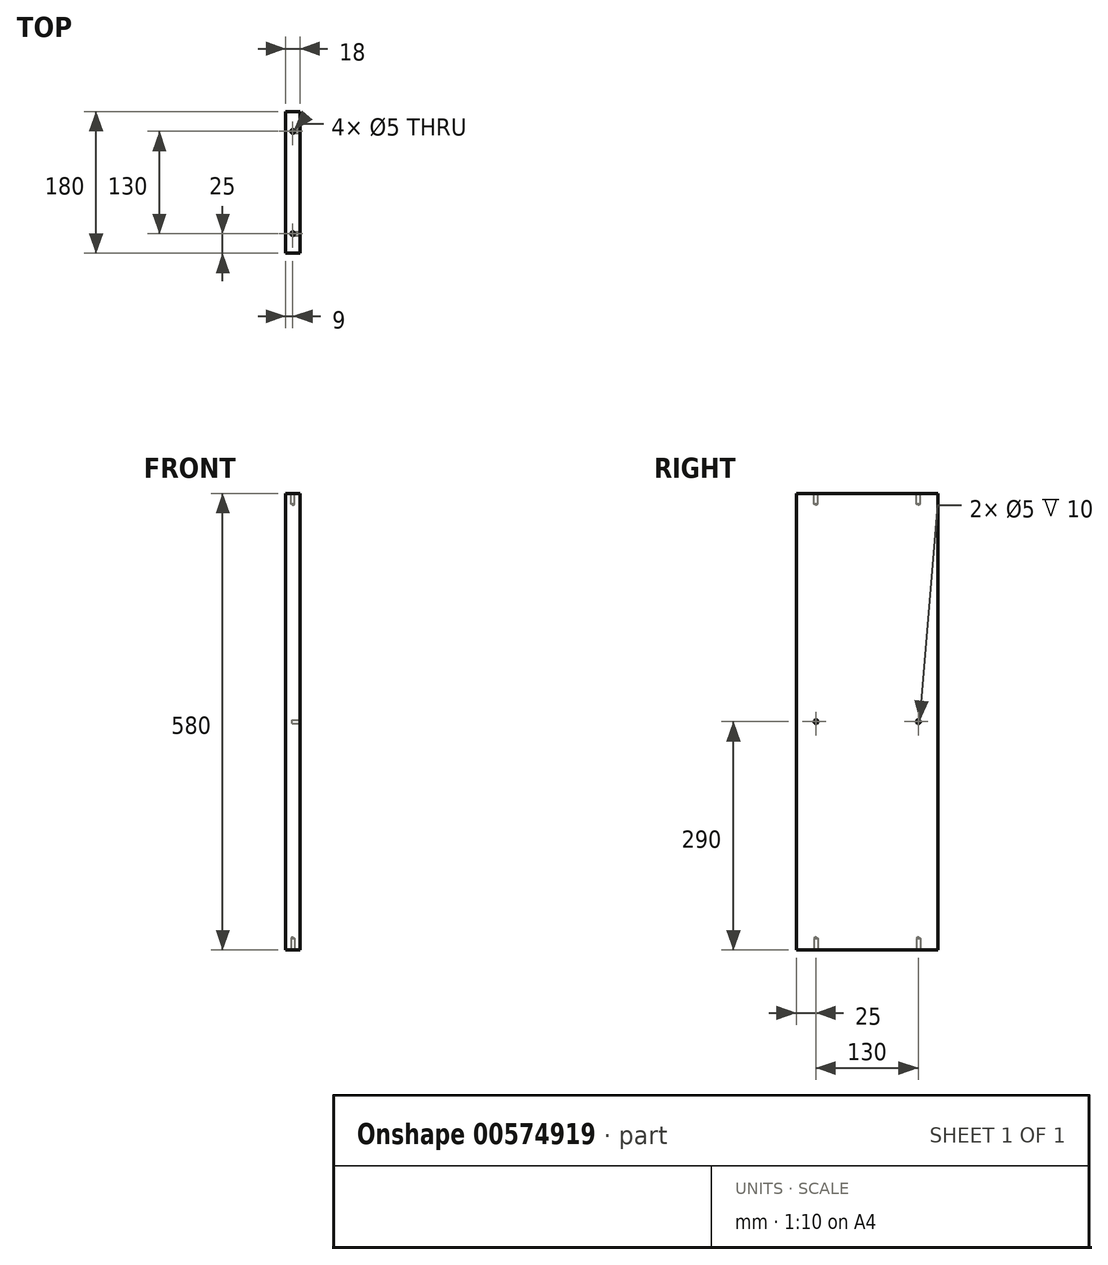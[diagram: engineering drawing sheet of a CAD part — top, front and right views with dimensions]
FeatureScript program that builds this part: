
annotation { "Feature Type Name" : "Feature", "Feature Type Description" : "" }
export const myFeature = defineFeature(function(context is Context, id is Id, definition is map)
    precondition{}
    {
        {
            var Q0;
            Q0=qCreatedBy(makeId("Front.planeOp"),FACE);
            var sketch = newSketch(context, id + "F0", { "sketchPlane" : qUnion([Q0])});
            skLineSegment(sketch, "E0.bottom", {"start": v(9, 290) * mm, "end": v(-9, 290) * mm});
            skLineSegment(sketch, "E0.top", {"start": v(9, -290) * mm, "end": v(-9, -290) * mm});
            skLineSegment(sketch, "E0.left", {"start": v(9, 290) * mm, "end": v(9, -290) * mm});
            skLineSegment(sketch, "E0.right", {"start": v(-9, 290) * mm, "end": v(-9, -290) * mm});
            skPoint(sketch, "E0.middle", {"position": v(0, 0) * mm});
            skSolve(sketch);
        }
        {
            var Q0;
            Q0 = qSketchRegion(id + "F0", true);
            extrude(context, id + "F1", {"entities" : qUnion([Q0]), "depth" : 180 * mm, "offsetDistance" : 25 * mm, "symmetric" : true});
        }
        {
            var Q0;
            Q0=makeQuery(id+"F1.opExtrude","SWEPT_FACE",FACE,{"disambiguationData":[OSD([sQuery(id+"F0.wireOp",EDGE,"E0.bottom")])]});
            var sketch = newSketch(context, id + "F2", { "sketchPlane" : qUnion([Q0])});
            skPoint(sketch, "E1", {"position": v(0, -65) * mm});
            skPoint(sketch, "E2", {"position": v(0, 65) * mm});
            skSolve(sketch);
        }
        {
            var Q0;
            Q0=sQuery(id+"F2.wireOp",VERTEX,"E2");
            var Q1;
            Q1=sQuery(id+"F2.wireOp",VERTEX,"E1");
            var Q2;
            Q2=makeQuery(id+"F1.opExtrude","SWEPT_BODY",BODY,{"disambiguationData":[OSD([sQuery(id+"F0.wireOp",EDGE,"E0.bottom"),sQuery(id+"F0.wireOp",EDGE,"E0.top"),sQuery(id+"F0.wireOp",EDGE,"E0.left"),sQuery(id+"F0.wireOp",EDGE,"E0.right")])]});
            hole(context, id + "F3", {"style" : HoleStyle.SIMPLE, "endStyle" : HoleEndStyle.BLIND, "holeDiameter" : 5 * mm, "holeDepth" : 13.5 * mm, "isTappedThrough" : true, "tappedDepth" : 12 * mm, "tapClearance" : 3, "locations" : qUnion([Q0, Q1]), "scope" : qUnion([Q2])});
        }
        {
            var Q0;
            Q0=makeQuery(id+"F1.opExtrude","SWEPT_FACE",FACE,{"disambiguationData":[OSD([sQuery(id+"F0.wireOp",EDGE,"E0.top")])]});
            var sketch = newSketch(context, id + "F4", { "sketchPlane" : qUnion([Q0])});
            skPoint(sketch, "E3", {"position": v(0, 65) * mm});
            skPoint(sketch, "E4", {"position": v(0, -65) * mm});
            skSolve(sketch);
        }
        {
            var Q0;
            Q0=sQuery(id+"F4.wireOp",VERTEX,"E3");
            var Q1;
            Q1=sQuery(id+"F4.wireOp",VERTEX,"E4");
            var Q2;
            Q2=makeQuery(id+"F1.opExtrude","SWEPT_BODY",BODY,{"disambiguationData":[OSD([sQuery(id+"F0.wireOp",EDGE,"E0.bottom"),sQuery(id+"F0.wireOp",EDGE,"E0.top"),sQuery(id+"F0.wireOp",EDGE,"E0.left"),sQuery(id+"F0.wireOp",EDGE,"E0.right")])]});
            hole(context, id + "F5", {"style" : HoleStyle.SIMPLE, "endStyle" : HoleEndStyle.BLIND, "holeDiameter" : 5 * mm, "holeDepth" : 15 * mm, "isTappedThrough" : true, "tappedDepth" : 12 * mm, "tapClearance" : 3, "locations" : qUnion([Q0, Q1]), "scope" : qUnion([Q2])});
        }
        {
            var Q0;
            Q0=makeQuery(id+"F1.opExtrude","SWEPT_FACE",FACE,{"disambiguationData":[OSD([sQuery(id+"F0.wireOp",EDGE,"E0.left")])]});
            var sketch = newSketch(context, id + "F6", { "sketchPlane" : qUnion([Q0])});
            skCircle(sketch, "E5", {"center": v(-60, 0) * mm, "radius": 2.5 * mm});
            skCircle(sketch, "E6", {"center": v(60, 0) * mm, "radius": 2.5 * mm});
            skSolve(sketch);
        }
        {
            var Q0;
            Q0=makeQuery(id+"F6.imprint","IMPRINT",FACE,{"disambiguationData":[TD([[makeQuery(id+"F6.imprint","IMPRINT",EDGE,{"derivedFrom":sQuery(id+"F6.wireOp",EDGE,"E5")}),-1.0]])]});
            extrude(context, id + "F7", {"entities" : qUnion([Q0]), "operationType" : NewBodyOperationType.REMOVE, "depth" : 10 * mm, "offsetDistance" : 25 * mm});
        }
        {
            var Q0;
            Q0=makeQuery(id+"F1.opExtrude","SWEPT_FACE",FACE,{"disambiguationData":[OSD([sQuery(id+"F0.wireOp",EDGE,"E0.left")])]});
            var sketch = newSketch(context, id + "F8", { "sketchPlane" : qUnion([Q0])});
            skCircle(sketch, "E7", {"center": v(-65, 0) * mm, "radius": 2.5 * mm});
            skCircle(sketch, "E8", {"center": v(65, 0) * mm, "radius": 2.5 * mm});
            skSolve(sketch);
        }
        {
            var Q0;
            Q0 = qSketchRegion(id + "F8", true);
            extrude(context, id + "F9", {"entities" : qUnion([Q0]), "operationType" : NewBodyOperationType.REMOVE, "oppositeDirection" : true, "depth" : 10 * mm, "offsetDistance" : 25 * mm});
        }
    });
